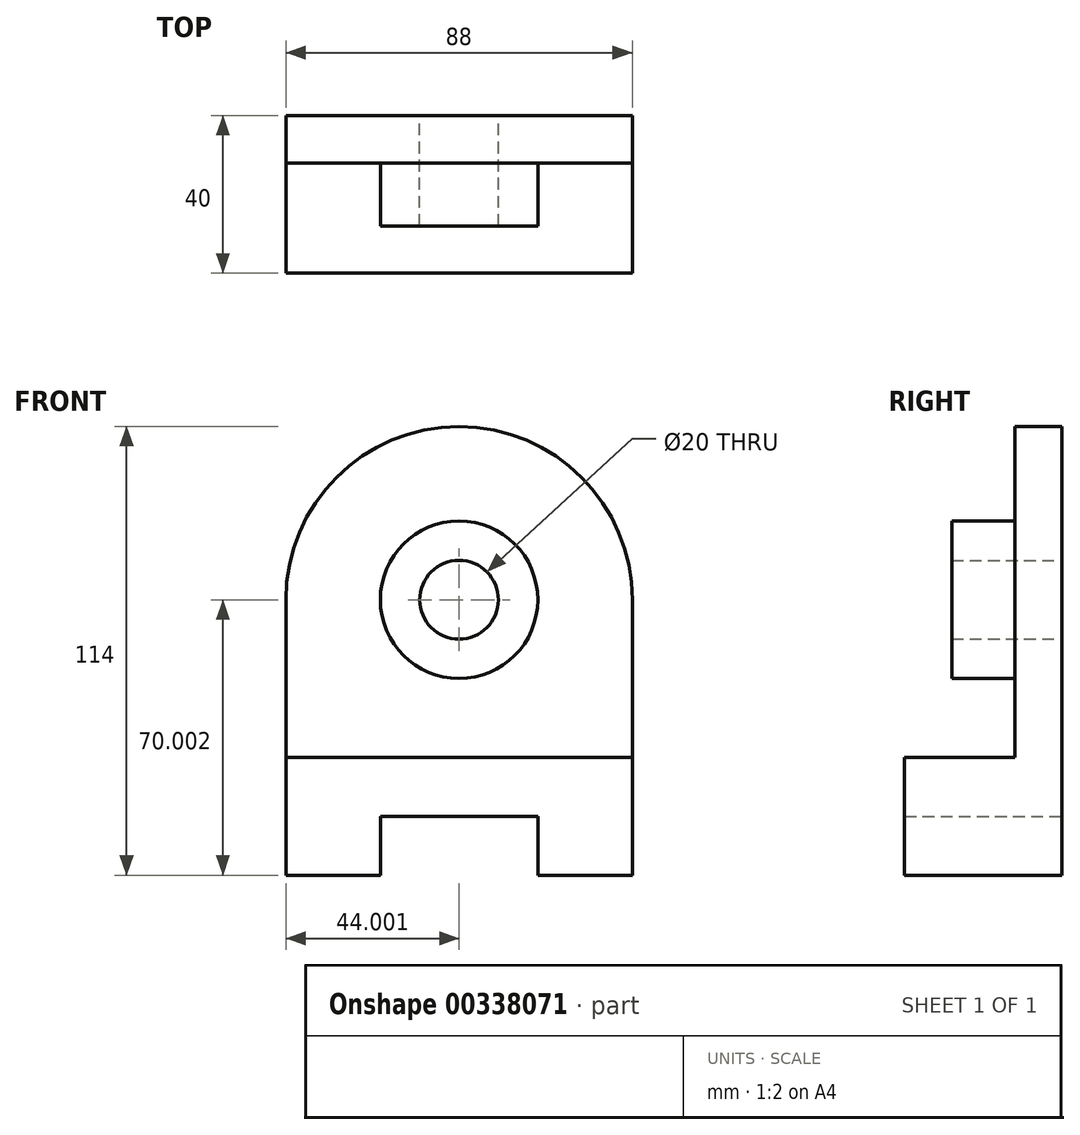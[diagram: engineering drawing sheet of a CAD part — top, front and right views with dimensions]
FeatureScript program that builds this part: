
annotation { "Feature Type Name" : "Feature", "Feature Type Description" : "" }
export const myFeature = defineFeature(function(context is Context, id is Id, definition is map)
    precondition{}
    {
        {
            var Q0;
            Q0=qCreatedBy(makeId("Front.planeOp"),FACE);
            var sketch = newSketch(context, id + "F0", { "sketchPlane" : qUnion([Q0])});
            skLineSegment(sketch, "E0", {"start": v(21.64, -19.57) * mm, "end": v(-2.36, -19.57) * mm});
            skLineSegment(sketch, "E1", {"start": v(-2.36, -19.57) * mm, "end": v(-2.36, 10.43) * mm});
            skLineSegment(sketch, "E2", {"start": v(-2.36, 10.43) * mm, "end": v(85.64, 10.43) * mm});
            skLineSegment(sketch, "E3", {"start": v(85.64, 10.43) * mm, "end": v(85.64, -19.57) * mm});
            skLineSegment(sketch, "E4", {"start": v(85.64, -19.57) * mm, "end": v(61.64, -19.57) * mm});
            skLineSegment(sketch, "E5", {"start": v(61.64, -19.57) * mm, "end": v(61.64, -4.57) * mm});
            skLineSegment(sketch, "E6", {"start": v(21.64, -19.57) * mm, "end": v(21.64, -4.57) * mm});
            skLineSegment(sketch, "E7", {"start": v(21.64, -4.57) * mm, "end": v(61.64, -4.57) * mm});
            skLineSegment(sketch, "E8", {"start": v(-2.36, 10.43) * mm, "end": v(-2.36, 50.43) * mm});
            skLineSegment(sketch, "E9", {"start": v(85.64, 10.43) * mm, "end": v(85.64, 50.43) * mm});
            skArc(sketch, "E10", {"start": v(85.64, 50.43) * mm, "mid": v(41.64, 94.43) * mm, "end": v(-2.36, 50.43) * mm});
            skCircle(sketch, "E11", {"center": v(41.64, 50.43) * mm, "radius": 20 * mm});
            skCircle(sketch, "E12", {"center": v(41.64, 50.43) * mm, "radius": 10 * mm});
            skSolve(sketch);
        }
        {
            var Q0;
            Q0=makeQuery(id+"F0.imprint","IMPRINT",FACE,{"disambiguationData":[TD([[makeQuery(id+"F0.imprint","IMPRINT",EDGE,{"derivedFrom":sQuery(id+"F0.wireOp",EDGE,"E2")}),1.0]])]});
            extrude(context, id + "F1", {"entities" : qUnion([Q0]), "depth" : 12 * mm});
        }
        {
            var Q0;
            Q0=makeQuery(id+"F0.imprint","IMPRINT",FACE,{"disambiguationData":[TD([[makeQuery(id+"F0.imprint","IMPRINT",EDGE,{"derivedFrom":sQuery(id+"F0.wireOp",EDGE,"E0")}),-1.0]])]});
            extrude(context, id + "F2", {"entities" : qUnion([Q0]), "operationType" : NewBodyOperationType.ADD, "depth" : 40 * mm});
        }
        {
            var Q0;
            Q0=makeQuery(id+"F0.imprint","IMPRINT",FACE,{"disambiguationData":[TD([[makeQuery(id+"F0.imprint","IMPRINT",EDGE,{"derivedFrom":sQuery(id+"F0.wireOp",EDGE,"E11")}),1.0]])]});
            extrude(context, id + "F3", {"entities" : qUnion([Q0]), "operationType" : NewBodyOperationType.ADD, "depth" : 28 * mm});
        }
    });
